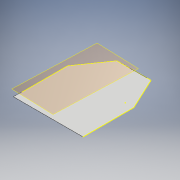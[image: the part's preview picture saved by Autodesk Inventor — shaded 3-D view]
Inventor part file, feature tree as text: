
AUTODESK INVENTOR PART (.ipt)
format: ipt  version: 2018 (Build 220112000, 112)  size: 119,808 bytes
history: native  units: mm
features: reference x11, other x6, sketch x2, plane x1, extrude x1
ambient origin geometry x8: Origin, YZ Plane, XZ Plane, XY Plane, X Axis, Y Axis, Z Axis, Center Point
bodies: Solid1 (feature_tree)
feature tree (21):
  other  "Table"
  other  "cover end plates-01"
  other  "cover end plates-02"
  plane  "Work Plane1"
  sketch  "Sketch1"  dims[d0=1.6mm d1=0.0mm]
  extrude  "Extrusion1"  [1 undecoded]
  reference  "Reference1"
  reference  "Reference2"
  reference  "Reference3"
  reference  "Reference4"
  reference  "Reference5"
  reference  "Reference6"
  sketch  "Sketch2"
  reference  "Reference7"
  reference  "Reference8"
  reference  "Reference9"
  reference  "Reference10"
  reference  "Reference11"
  other  "Lathe Model 2018.iam"
  other  "polycarbonate cover:1"
  other  "back plate:1"
note: 1 required parameter value undecoded (feature->parameter linkage not recoverable at this tier; creation-order binding heuristic only, values carry confidence <= 0.55)
